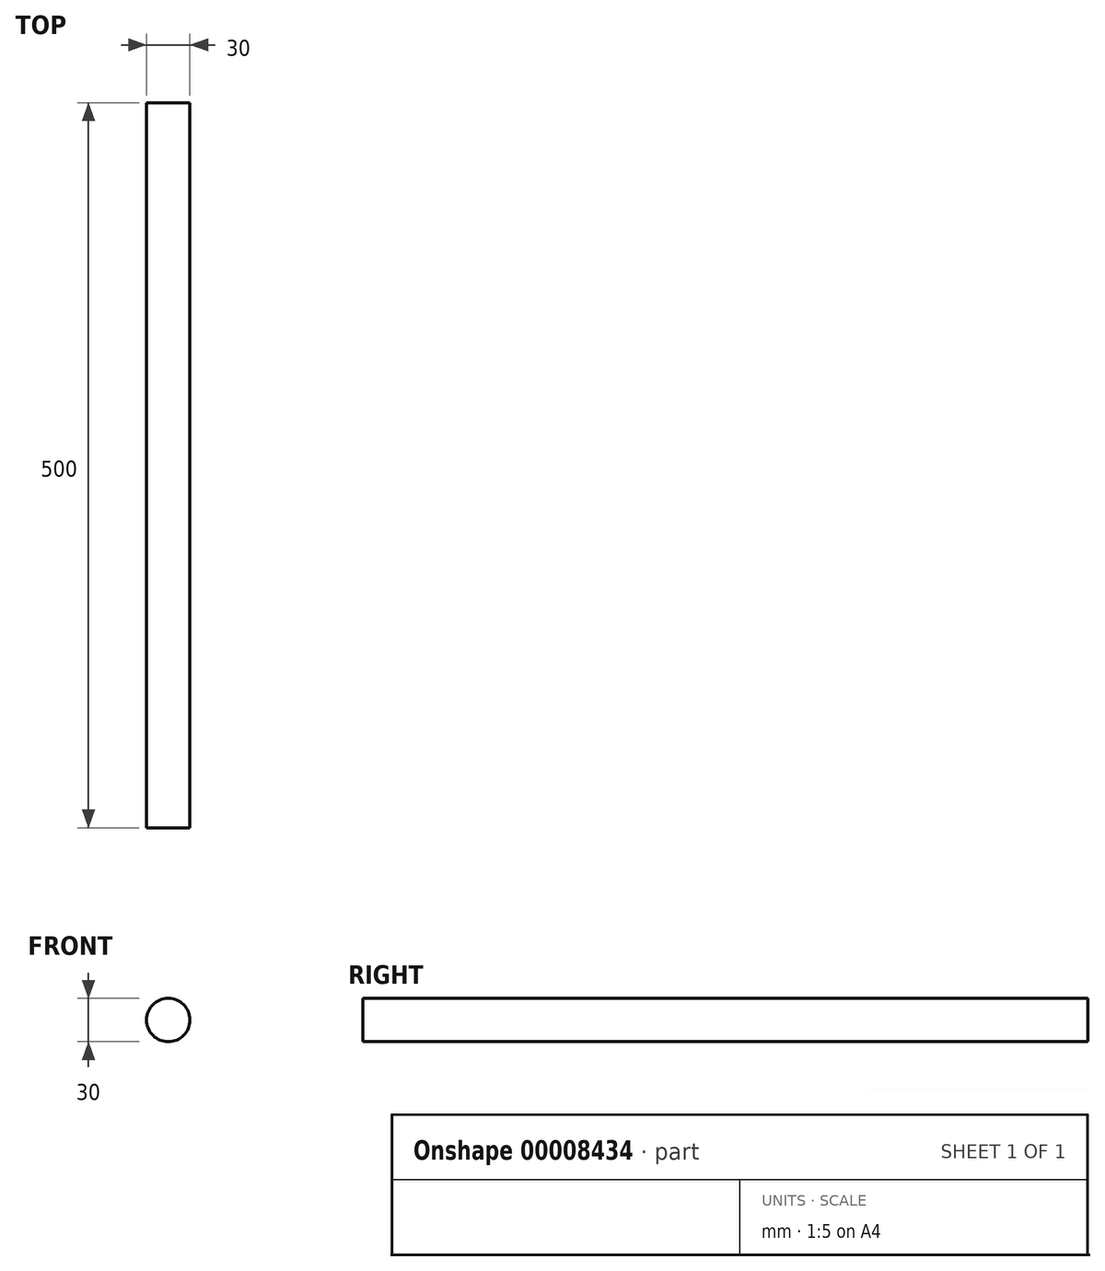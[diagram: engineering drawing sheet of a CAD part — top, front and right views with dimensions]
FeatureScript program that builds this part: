
annotation { "Feature Type Name" : "Feature", "Feature Type Description" : "" }
export const myFeature = defineFeature(function(context is Context, id is Id, definition is map)
    precondition{}
    {
        {
            var Q0;
            Q0=qCreatedBy(makeId("Front.planeOp"),FACE);
            var sketch = newSketch(context, id + "F0", { "sketchPlane" : qUnion([Q0])});
            skCircle(sketch, "E0", {"center": v(0, 0) * mm, "radius": 15 * mm});
            skSolve(sketch);
        }
        {
            var Q0;
            Q0 = qSketchRegion(id + "F0", true);
            extrude(context, id + "F1", {"entities" : qUnion([Q0]), "depth" : 500 * mm});
        }
    });
